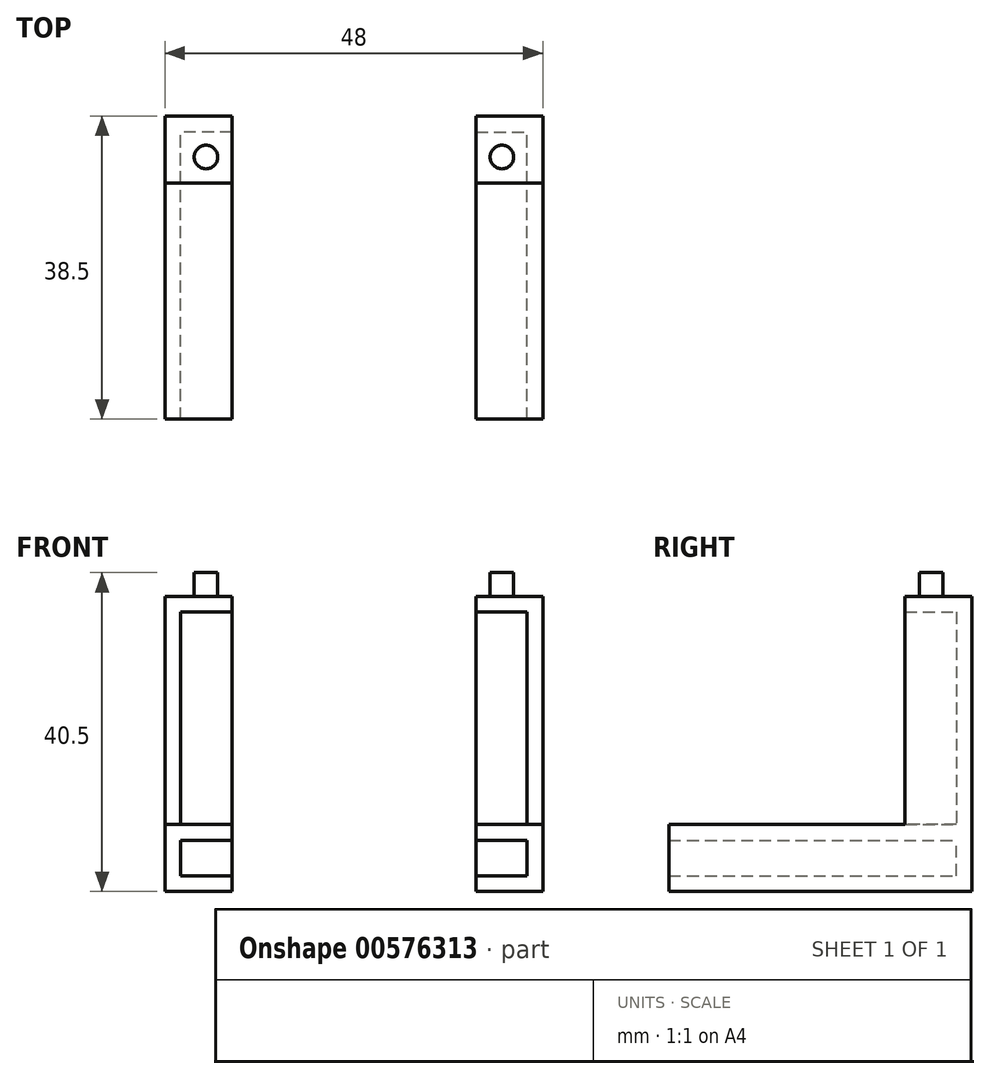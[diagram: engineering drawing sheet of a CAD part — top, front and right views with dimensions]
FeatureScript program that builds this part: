
annotation { "Feature Type Name" : "Feature", "Feature Type Description" : "" }
export const myFeature = defineFeature(function(context is Context, id is Id, definition is map)
    precondition{}
    {
        {
            var Q0;
            Q0=qCreatedBy(makeId("Top.planeOp"),FACE);
            var sketch = newSketch(context, id + "F0", { "sketchPlane" : qUnion([Q0])});
            skPoint(sketch, "E0.visualSharp", {"position": v(-21.27, 21.02) * mm});
            skPoint(sketch, "E1.visualSharp", {"position": v(22.73, 21.02) * mm});
            skPoint(sketch, "E2.visualSharp", {"position": v(-23.27, 23.02) * mm});
            skArc(sketch, "E2.filletArc", {"start": v(-16.77, 23.02) * mm, "mid": v(-21.37, 21.11) * mm, "end": v(-23.27, 16.52) * mm});
            skPoint(sketch, "E3.visualSharp", {"position": v(24.73, 23.02) * mm});
            skArc(sketch, "E3.filletArc", {"start": v(24.73, 16.52) * mm, "mid": v(22.82, 21.11) * mm, "end": v(18.23, 23.02) * mm});
            skLineSegment(sketch, "E4", {"start": v(-23.27, 14.52) * mm, "end": v(-21.27, 14.52) * mm});
            skLineSegment(sketch, "E5", {"start": v(-14.77, 23.02) * mm, "end": v(-14.77, 21.02) * mm});
            skLineSegment(sketch, "E6", {"start": v(16.23, 23.02) * mm, "end": v(16.23, 21.02) * mm});
            skLineSegment(sketch, "E7", {"start": v(22.73, 14.52) * mm, "end": v(24.73, 14.52) * mm});
            skLineSegment(sketch, "E8", {"start": v(-16.77, 23.02) * mm, "end": v(-14.77, 23.02) * mm});
            skLineSegment(sketch, "E9", {"start": v(-14.77, 21.02) * mm, "end": v(-16.77, 21.02) * mm});
            skLineSegment(sketch, "E10", {"start": v(-21.27, 14.52) * mm, "end": v(-21.27, 16.52) * mm});
            skLineSegment(sketch, "E11", {"start": v(-23.27, 14.52) * mm, "end": v(-23.27, 16.52) * mm});
            skLineSegment(sketch, "E12", {"start": v(16.23, 23.02) * mm, "end": v(18.23, 23.02) * mm});
            skLineSegment(sketch, "E13", {"start": v(16.23, 21.02) * mm, "end": v(18.23, 21.02) * mm});
            skLineSegment(sketch, "E14", {"start": v(22.73, 16.52) * mm, "end": v(22.73, 14.52) * mm});
            skLineSegment(sketch, "E15", {"start": v(24.73, 16.52) * mm, "end": v(24.73, 14.52) * mm});
            skLineSegment(sketch, "E16", {"start": v(-14.77, 23.02) * mm, "end": v(-23.27, 23.02) * mm});
            skLineSegment(sketch, "E17", {"start": v(-23.27, 16.52) * mm, "end": v(-23.27, 23.02) * mm});
            skLineSegment(sketch, "E18", {"start": v(18.23, 23.02) * mm, "end": v(24.73, 23.02) * mm});
            skLineSegment(sketch, "E19", {"start": v(24.73, 16.52) * mm, "end": v(24.73, 23.02) * mm});
            skLineSegment(sketch, "E20", {"start": v(18.23, 21.02) * mm, "end": v(22.73, 21.02) * mm});
            skLineSegment(sketch, "E21", {"start": v(22.73, 16.52) * mm, "end": v(22.73, 21.02) * mm});
            skLineSegment(sketch, "E22", {"start": v(-16.77, 21.02) * mm, "end": v(-21.27, 21.02) * mm});
            skLineSegment(sketch, "E23", {"start": v(-21.27, 16.52) * mm, "end": v(-21.27, 21.02) * mm});
            skSolve(sketch);
        }
        {
            var Q0;
            Q0 = qSketchRegion(id + "F0", true);
            extrude(context, id + "F1", {"entities" : qUnion([Q0]), "depth" : 31 * mm, "offsetDistance" : 25 * mm});
        }
        {
            var Q0;
            Q0=makeQuery(id+"F1.opExtrude","CAP_FACE",FACE,{"disambiguationData":[OSD([sQuery(id+"F0.wireOp",EDGE,"E0.filletArc"),sQuery(id+"F0.wireOp",EDGE,"E2.filletArc"),sQuery(id+"F0.wireOp",EDGE,"E4"),sQuery(id+"F0.wireOp",EDGE,"E5"),sQuery(id+"F0.wireOp",EDGE,"E8"),sQuery(id+"F0.wireOp",EDGE,"E9"),sQuery(id+"F0.wireOp",EDGE,"E10"),sQuery(id+"F0.wireOp",EDGE,"E11")])],"isStart":true});
            var sketch = newSketch(context, id + "F2", { "sketchPlane" : qUnion([Q0])});
            skLineSegment(sketch, "E24", {"start": v(-14.77, -21.02) * mm, "end": v(-14.77, -14.52) * mm});
            skLineSegment(sketch, "E25", {"start": v(-21.27, -14.52) * mm, "end": v(-14.77, -14.52) * mm});
            skSolve(sketch);
        }
        {
            var Q0;
            Q0=makeQuery(id+"F2.imprint","IMPRINT",FACE,{"disambiguationData":[TD([[makeQuery(id+"F2.imprint","IMPRINT",EDGE,{"derivedFrom":sQuery(id+"F2.wireOp",EDGE,"E24")}),1.0]])]});
            extrude(context, id + "F3", {"entities" : qUnion([Q0]), "operationType" : NewBodyOperationType.ADD, "oppositeDirection" : true, "depth" : 2 * mm, "offsetDistance" : 25 * mm});
        }
        {
            var Q0;
            Q0=makeQuery(id+"F1.opExtrude","CAP_FACE",FACE,{"disambiguationData":[OSD([sQuery(id+"F0.wireOp",EDGE,"E1.filletArc"),sQuery(id+"F0.wireOp",EDGE,"E3.filletArc"),sQuery(id+"F0.wireOp",EDGE,"E6"),sQuery(id+"F0.wireOp",EDGE,"E7"),sQuery(id+"F0.wireOp",EDGE,"E12"),sQuery(id+"F0.wireOp",EDGE,"E13"),sQuery(id+"F0.wireOp",EDGE,"E14"),sQuery(id+"F0.wireOp",EDGE,"E15")])],"isStart":true});
            var sketch = newSketch(context, id + "F4", { "sketchPlane" : qUnion([Q0])});
            skLineSegment(sketch, "E26", {"start": v(16.23, -21.02) * mm, "end": v(16.23, -14.52) * mm});
            skLineSegment(sketch, "E27", {"start": v(16.23, -14.52) * mm, "end": v(22.73, -14.52) * mm});
            skSolve(sketch);
        }
        {
            var Q0;
            Q0=makeQuery(id+"F4.imprint","IMPRINT",FACE,{"disambiguationData":[TD([[makeQuery(id+"F4.imprint","IMPRINT",EDGE,{"derivedFrom":sQuery(id+"F4.wireOp",EDGE,"E26")}),-1.0]])]});
            extrude(context, id + "F5", {"entities" : qUnion([Q0]), "operationType" : NewBodyOperationType.ADD, "oppositeDirection" : true, "depth" : 2 * mm, "offsetDistance" : 25 * mm});
        }
        {
            var Q0;
            Q0 = qSketchRegion(id + "F0", true);
            extrude(context, id + "F6", {"entities" : qUnion([Q0]), "operationType" : NewBodyOperationType.ADD, "oppositeDirection" : true, "depth" : 6.5 * mm, "offsetDistance" : 25 * mm});
        }
        {
            var Q0;
            Q0=makeQuery(id+"F6.opExtrude","CAP_FACE",FACE,{"disambiguationData":[OSD([sQuery(id+"F0.wireOp",EDGE,"E0.filletArc"),sQuery(id+"F0.wireOp",EDGE,"E2.filletArc"),sQuery(id+"F0.wireOp",EDGE,"E4"),sQuery(id+"F0.wireOp",EDGE,"E5"),sQuery(id+"F0.wireOp",EDGE,"E8"),sQuery(id+"F0.wireOp",EDGE,"E9"),sQuery(id+"F0.wireOp",EDGE,"E10"),sQuery(id+"F0.wireOp",EDGE,"E11")])],"isStart":false});
            var sketch = newSketch(context, id + "F7", { "sketchPlane" : qUnion([Q0])});
            skLineSegment(sketch, "E28", {"start": v(-21.27, -14.52) * mm, "end": v(-14.77, -14.52) * mm});
            skLineSegment(sketch, "E29", {"start": v(-14.77, -14.52) * mm, "end": v(-14.77, -21.02) * mm});
            skSolve(sketch);
        }
        {
            var Q0;
            Q0=makeQuery(id+"F7.imprint","IMPRINT",FACE,{"disambiguationData":[TD([[makeQuery(id+"F7.imprint","IMPRINT",EDGE,{"derivedFrom":sQuery(id+"F7.wireOp",EDGE,"E28")}),-1.0]])]});
            extrude(context, id + "F8", {"entities" : qUnion([Q0]), "operationType" : NewBodyOperationType.ADD, "oppositeDirection" : true, "depth" : 2 * mm, "offsetDistance" : 25 * mm});
        }
        {
            var Q0;
            Q0=makeQuery(id+"F6.opExtrude","CAP_FACE",FACE,{"disambiguationData":[OSD([sQuery(id+"F0.wireOp",EDGE,"E1.filletArc"),sQuery(id+"F0.wireOp",EDGE,"E3.filletArc"),sQuery(id+"F0.wireOp",EDGE,"E6"),sQuery(id+"F0.wireOp",EDGE,"E7"),sQuery(id+"F0.wireOp",EDGE,"E12"),sQuery(id+"F0.wireOp",EDGE,"E13"),sQuery(id+"F0.wireOp",EDGE,"E14"),sQuery(id+"F0.wireOp",EDGE,"E15")])],"isStart":false});
            var sketch = newSketch(context, id + "F9", { "sketchPlane" : qUnion([Q0])});
            skLineSegment(sketch, "E30", {"start": v(22.73, -14.52) * mm, "end": v(16.23, -14.52) * mm});
            skLineSegment(sketch, "E31", {"start": v(16.23, -14.52) * mm, "end": v(16.23, -21.02) * mm});
            skSolve(sketch);
        }
        {
            var Q0;
            Q0=makeQuery(id+"F9.imprint","IMPRINT",FACE,{"disambiguationData":[TD([[makeQuery(id+"F9.imprint","IMPRINT",EDGE,{"derivedFrom":sQuery(id+"F9.wireOp",EDGE,"E30")}),1.0]])]});
            extrude(context, id + "F10", {"entities" : qUnion([Q0]), "operationType" : NewBodyOperationType.ADD, "oppositeDirection" : true, "depth" : 2 * mm, "offsetDistance" : 25 * mm});
        }
        {
            var Q0;
            Q0=makeQuery(id+"F1.opExtrude","CAP_FACE",FACE,{"disambiguationData":[OSD([sQuery(id+"F0.wireOp",EDGE,"E1.filletArc"),sQuery(id+"F0.wireOp",EDGE,"E3.filletArc"),sQuery(id+"F0.wireOp",EDGE,"E6"),sQuery(id+"F0.wireOp",EDGE,"E7"),sQuery(id+"F0.wireOp",EDGE,"E12"),sQuery(id+"F0.wireOp",EDGE,"E13"),sQuery(id+"F0.wireOp",EDGE,"E14"),sQuery(id+"F0.wireOp",EDGE,"E15")])],"isStart":false});
            var sketch = newSketch(context, id + "F11", { "sketchPlane" : qUnion([Q0])});
            skLineSegment(sketch, "E32", {"start": v(16.23, 21.02) * mm, "end": v(16.23, 14.52) * mm});
            skLineSegment(sketch, "E33", {"start": v(16.23, 14.52) * mm, "end": v(22.73, 14.52) * mm});
            skSolve(sketch);
        }
        {
            var Q0;
            Q0=makeQuery(id+"F11.imprint","IMPRINT",FACE,{"disambiguationData":[TD([[makeQuery(id+"F11.imprint","IMPRINT",EDGE,{"derivedFrom":sQuery(id+"F11.wireOp",EDGE,"E32")}),1.0]])]});
            extrude(context, id + "F12", {"entities" : qUnion([Q0]), "operationType" : NewBodyOperationType.ADD, "oppositeDirection" : true, "depth" : 2 * mm, "offsetDistance" : 25 * mm});
        }
        {
            var Q0;
            Q0=makeQuery(id+"F1.opExtrude","CAP_FACE",FACE,{"disambiguationData":[OSD([sQuery(id+"F0.wireOp",EDGE,"E0.filletArc"),sQuery(id+"F0.wireOp",EDGE,"E2.filletArc"),sQuery(id+"F0.wireOp",EDGE,"E4"),sQuery(id+"F0.wireOp",EDGE,"E5"),sQuery(id+"F0.wireOp",EDGE,"E8"),sQuery(id+"F0.wireOp",EDGE,"E9"),sQuery(id+"F0.wireOp",EDGE,"E10"),sQuery(id+"F0.wireOp",EDGE,"E11")])],"isStart":false});
            var sketch = newSketch(context, id + "F13", { "sketchPlane" : qUnion([Q0])});
            skLineSegment(sketch, "E34", {"start": v(-14.77, 21.02) * mm, "end": v(-14.77, 14.52) * mm});
            skLineSegment(sketch, "E35", {"start": v(-14.77, 14.52) * mm, "end": v(-21.27, 14.52) * mm});
            skSolve(sketch);
        }
        {
            var Q0;
            Q0=makeQuery(id+"F13.imprint","IMPRINT",FACE,{"disambiguationData":[TD([[makeQuery(id+"F13.imprint","IMPRINT",EDGE,{"derivedFrom":sQuery(id+"F13.wireOp",EDGE,"E34")}),-1.0]])]});
            extrude(context, id + "F14", {"entities" : qUnion([Q0]), "operationType" : NewBodyOperationType.ADD, "oppositeDirection" : true, "depth" : 2 * mm, "offsetDistance" : 25 * mm});
        }
        {
            var Q0;
            {var subQ0=sQuery(id+"F0.wireOp",EDGE,"E10");var subQ1=sQuery(id+"F0.wireOp",EDGE,"E9");var subQ2=sQuery(id+"F0.wireOp",EDGE,"E0.filletArc");Q0=makeQuery(id+"F14.boolean.opBoolean","MERGE",FACE,{"derivedFrom":[makeQuery(id+"F1.opExtrude","CAP_FACE",FACE,{"disambiguationData":[OSD([subQ2,sQuery(id+"F0.wireOp",EDGE,"E2.filletArc"),sQuery(id+"F0.wireOp",EDGE,"E4"),sQuery(id+"F0.wireOp",EDGE,"E5"),sQuery(id+"F0.wireOp",EDGE,"E8"),subQ1,subQ0,sQuery(id+"F0.wireOp",EDGE,"E11")])],"isStart":false}),makeQuery(id+"F14.opExtrude","CAP_FACE",FACE,{"disambiguationData":[OSD([subQ2,subQ1,subQ0,sQuery(id+"F13.wireOp",EDGE,"E34"),sQuery(id+"F13.wireOp",EDGE,"E35")])],"isStart":true})]});}
            var sketch = newSketch(context, id + "F15", { "sketchPlane" : qUnion([Q0])});
            skCircle(sketch, "E36", {"center": v(-18.07, 17.81) * mm, "radius": 1.5 * mm});
            skSolve(sketch);
        }
        {
            var Q0;
            Q0=makeQuery(id+"F15.imprint","IMPRINT",FACE,{"disambiguationData":[TD([[makeQuery(id+"F15.imprint","IMPRINT",EDGE,{"derivedFrom":sQuery(id+"F15.wireOp",EDGE,"E36")}),1.0]])]});
            extrude(context, id + "F16", {"entities" : qUnion([Q0]), "operationType" : NewBodyOperationType.ADD, "depth" : 3 * mm, "offsetDistance" : 25 * mm});
        }
        {
            var Q0;
            {var subQ0=sQuery(id+"F0.wireOp",EDGE,"E14");var subQ1=sQuery(id+"F0.wireOp",EDGE,"E13");var subQ2=sQuery(id+"F0.wireOp",EDGE,"E1.filletArc");Q0=makeQuery(id+"F12.boolean.opBoolean","MERGE",FACE,{"derivedFrom":[makeQuery(id+"F1.opExtrude","CAP_FACE",FACE,{"disambiguationData":[OSD([subQ2,sQuery(id+"F0.wireOp",EDGE,"E3.filletArc"),sQuery(id+"F0.wireOp",EDGE,"E6"),sQuery(id+"F0.wireOp",EDGE,"E7"),sQuery(id+"F0.wireOp",EDGE,"E12"),subQ1,subQ0,sQuery(id+"F0.wireOp",EDGE,"E15")])],"isStart":false}),makeQuery(id+"F12.opExtrude","CAP_FACE",FACE,{"disambiguationData":[OSD([subQ2,subQ1,subQ0,sQuery(id+"F11.wireOp",EDGE,"E32"),sQuery(id+"F11.wireOp",EDGE,"E33")])],"isStart":true})]});}
            var sketch = newSketch(context, id + "F17", { "sketchPlane" : qUnion([Q0])});
            skCircle(sketch, "E37", {"center": v(19.52, 17.81) * mm, "radius": 1.5 * mm});
            skSolve(sketch);
        }
        {
            var Q0;
            Q0=makeQuery(id+"F17.imprint","IMPRINT",FACE,{"disambiguationData":[TD([[makeQuery(id+"F17.imprint","IMPRINT",EDGE,{"derivedFrom":sQuery(id+"F17.wireOp",EDGE,"E37")}),1.0]])]});
            extrude(context, id + "F18", {"entities" : qUnion([Q0]), "operationType" : NewBodyOperationType.ADD, "depth" : 3 * mm, "offsetDistance" : 25 * mm});
        }
        {
            var Q0;
            {var subQ0=sQuery(id+"F0.wireOp",EDGE,"E4");Q0=makeQuery(id+"F14.boolean.opBoolean","MERGE",FACE,{"derivedFrom":[makeQuery(id+"F8.boolean.opBoolean","MERGE",FACE,{"derivedFrom":[makeQuery(id+"F6.boolean.opBoolean","MERGE",FACE,{"derivedFrom":[makeQuery(id+"F3.boolean.opBoolean","MERGE",FACE,{"derivedFrom":[makeQuery(id+"F1.opExtrude","SWEPT_FACE",FACE,{"disambiguationData":[OSD([subQ0])]}),makeQuery(id+"F3.opExtrude","SWEPT_FACE",FACE,{"disambiguationData":[OSD([sQuery(id+"F2.wireOp",EDGE,"E25")])]})]}),makeQuery(id+"F6.opExtrude","SWEPT_FACE",FACE,{"disambiguationData":[OSD([subQ0])]})]}),makeQuery(id+"F8.opExtrude","SWEPT_FACE",FACE,{"disambiguationData":[OSD([sQuery(id+"F7.wireOp",EDGE,"E28")])]})]}),makeQuery(id+"F14.opExtrude","SWEPT_FACE",FACE,{"disambiguationData":[OSD([sQuery(id+"F13.wireOp",EDGE,"E35")])]})]});}
            var sketch = newSketch(context, id + "F19", { "sketchPlane" : qUnion([Q0])});
            skLineSegment(sketch, "E38", {"start": v(16.23, 2) * mm, "end": v(24.73, 2) * mm});
            skLineSegment(sketch, "E39", {"start": v(24.73, 2) * mm, "end": v(24.73, -6.5) * mm});
            skLineSegment(sketch, "E40", {"start": v(24.73, -6.5) * mm, "end": v(16.23, -6.5) * mm});
            skLineSegment(sketch, "E41", {"start": v(16.23, -6.5) * mm, "end": v(16.23, -4.5) * mm});
            skLineSegment(sketch, "E42", {"start": v(16.23, -4.5) * mm, "end": v(22.73, -4.5) * mm});
            skLineSegment(sketch, "E43", {"start": v(22.73, -4.5) * mm, "end": v(22.73, 0) * mm});
            skLineSegment(sketch, "E44", {"start": v(22.73, 0) * mm, "end": v(16.23, 0) * mm});
            skLineSegment(sketch, "E45", {"start": v(16.23, 0) * mm, "end": v(16.23, 2) * mm});
            skLineSegment(sketch, "E46", {"start": v(-14.77, 2) * mm, "end": v(-23.27, 2) * mm});
            skLineSegment(sketch, "E47", {"start": v(-23.27, 2) * mm, "end": v(-23.27, -6.5) * mm});
            skLineSegment(sketch, "E48", {"start": v(-23.27, -6.5) * mm, "end": v(-14.77, -6.5) * mm});
            skLineSegment(sketch, "E49", {"start": v(-14.77, -6.5) * mm, "end": v(-14.77, -4.5) * mm});
            skLineSegment(sketch, "E50", {"start": v(-14.77, -4.5) * mm, "end": v(-21.27, -4.5) * mm});
            skLineSegment(sketch, "E51", {"start": v(-21.27, -4.5) * mm, "end": v(-21.27, 0) * mm});
            skLineSegment(sketch, "E52", {"start": v(-21.27, 0) * mm, "end": v(-14.77, 0) * mm});
            skLineSegment(sketch, "E53", {"start": v(-14.77, 0) * mm, "end": v(-14.77, 2) * mm});
            skSolve(sketch);
        }
        {
            var Q0;
            {var subQ0=sQuery(id+"F19.wireOp",EDGE,"E47");Q0=makeQuery(id+"F19.imprint","IMPRINT",FACE,{"disambiguationData":[TD([[makeQuery(id+"F19.imprint","IMPRINT",EDGE,{"derivedFrom":subQ0}),1.0]])]});}
            extrude(context, id + "F20", {"entities" : qUnion([Q0]), "operationType" : NewBodyOperationType.ADD, "depth" : 30 * mm, "offsetDistance" : 25 * mm});
        }
        {
            var Q0;
            {var subQ0=sQuery(id+"F0.wireOp",EDGE,"E7");Q0=makeQuery(id+"F12.boolean.opBoolean","MERGE",FACE,{"derivedFrom":[makeQuery(id+"F10.boolean.opBoolean","MERGE",FACE,{"derivedFrom":[makeQuery(id+"F6.boolean.opBoolean","MERGE",FACE,{"derivedFrom":[makeQuery(id+"F5.boolean.opBoolean","MERGE",FACE,{"derivedFrom":[makeQuery(id+"F1.opExtrude","SWEPT_FACE",FACE,{"disambiguationData":[OSD([subQ0])]}),makeQuery(id+"F5.opExtrude","SWEPT_FACE",FACE,{"disambiguationData":[OSD([sQuery(id+"F4.wireOp",EDGE,"E27")])]})]}),makeQuery(id+"F6.opExtrude","SWEPT_FACE",FACE,{"disambiguationData":[OSD([subQ0])]})]}),makeQuery(id+"F10.opExtrude","SWEPT_FACE",FACE,{"disambiguationData":[OSD([sQuery(id+"F9.wireOp",EDGE,"E30")])]})]}),makeQuery(id+"F12.opExtrude","SWEPT_FACE",FACE,{"disambiguationData":[OSD([sQuery(id+"F11.wireOp",EDGE,"E33")])]})]});}
            var sketch = newSketch(context, id + "F21", { "sketchPlane" : qUnion([Q0])});
            skLineSegment(sketch, "E54", {"start": v(16.23, 2) * mm, "end": v(24.73, 2) * mm});
            skLineSegment(sketch, "E55", {"start": v(24.73, 2) * mm, "end": v(24.73, -6.5) * mm});
            skLineSegment(sketch, "E56", {"start": v(24.73, -6.5) * mm, "end": v(16.23, -6.5) * mm});
            skLineSegment(sketch, "E57", {"start": v(16.23, -6.5) * mm, "end": v(16.23, -4.5) * mm});
            skLineSegment(sketch, "E58", {"start": v(16.23, -4.5) * mm, "end": v(22.73, -4.5) * mm});
            skLineSegment(sketch, "E59", {"start": v(22.73, -4.5) * mm, "end": v(22.73, 0) * mm});
            skLineSegment(sketch, "E60", {"start": v(22.73, 0) * mm, "end": v(16.23, 0) * mm});
            skLineSegment(sketch, "E61", {"start": v(16.23, 0) * mm, "end": v(16.23, 2) * mm});
            skSolve(sketch);
        }
        {
            var Q0;
            {var subQ0=sQuery(id+"F21.wireOp",EDGE,"E55");Q0=makeQuery(id+"F21.imprint","IMPRINT",FACE,{"disambiguationData":[TD([[makeQuery(id+"F21.imprint","IMPRINT",EDGE,{"derivedFrom":subQ0}),-1.0]])]});}
            extrude(context, id + "F22", {"entities" : qUnion([Q0]), "operationType" : NewBodyOperationType.ADD, "depth" : 30 * mm, "offsetDistance" : 25 * mm});
        }
    });
